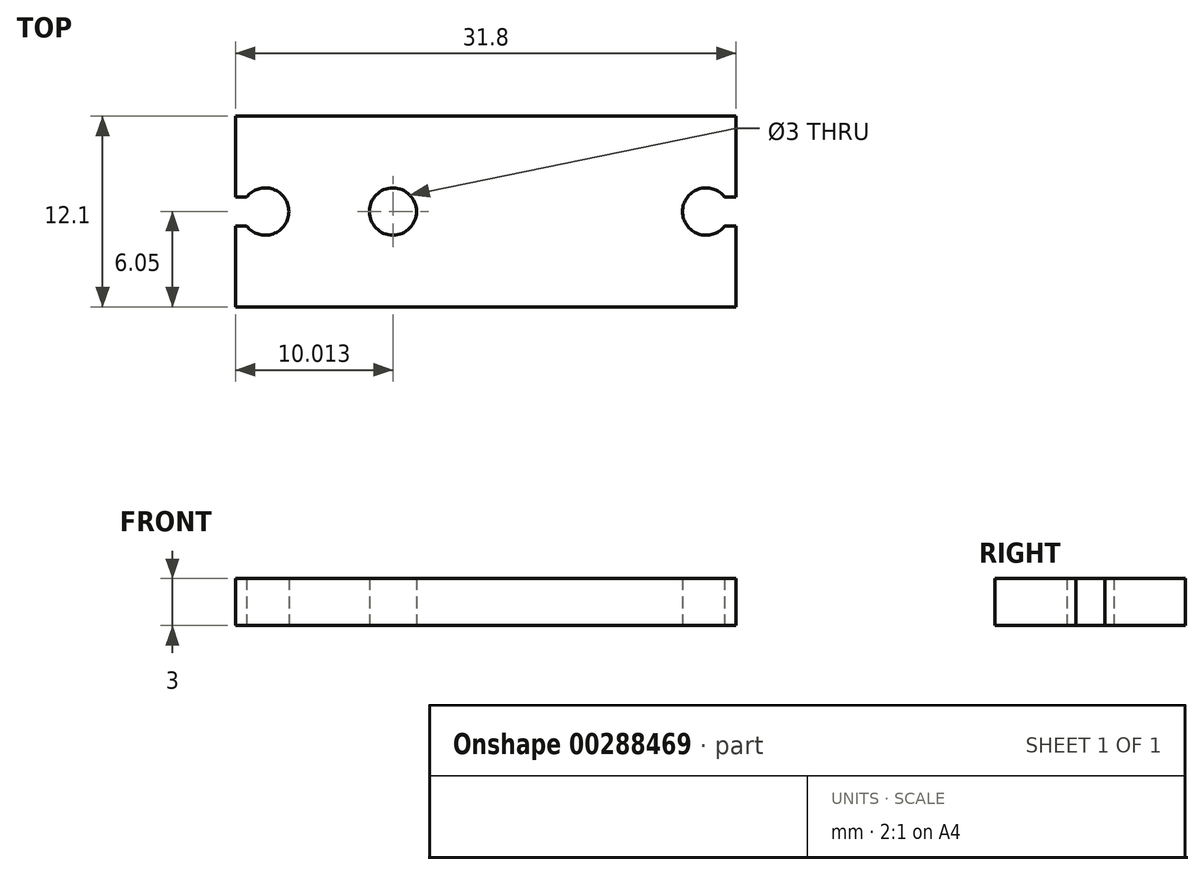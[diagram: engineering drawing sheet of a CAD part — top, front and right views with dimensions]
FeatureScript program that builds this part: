
annotation { "Feature Type Name" : "Feature", "Feature Type Description" : "" }
export const myFeature = defineFeature(function(context is Context, id is Id, definition is map)
    precondition{}
    {
        {
            var Q0;
            Q0=qCreatedBy(makeId("Top.planeOp"),FACE);
            var sketch = newSketch(context, id + "F0", { "sketchPlane" : qUnion([Q0])});
            skLineSegment(sketch, "E0.bottom", {"start": v(-15.9, 6.05) * mm, "end": v(15.9, 6.05) * mm});
            skLineSegment(sketch, "E0.top", {"start": v(-15.9, -6.05) * mm, "end": v(15.9, -6.05) * mm});
            skLineSegment(sketch, "E0.left", {"start": v(-15.9, 6.05) * mm, "end": v(-15.9, 0.93) * mm});
            skLineSegment(sketch, "E0.right", {"start": v(15.9, 6.05) * mm, "end": v(15.9, 0.93) * mm});
            skPoint(sketch, "E1", {"position": v(14, 0) * mm});
            skArc(sketch, "E2", {"start": v(15.18, 0.93) * mm, "mid": v(12.5, 0) * mm, "end": v(15.18, -0.93) * mm});
            skArc(sketch, "E3.MirrorC", {"start": v(-15.18, 0.93) * mm, "mid": v(-12.5, 0) * mm, "end": v(-15.18, -0.93) * mm});
            skPoint(sketch, "E4", {"position": v(-5.89, 0) * mm});
            skCircle(sketch, "E5", {"center": v(-5.89, 0) * mm, "radius": 1.5 * mm});
            skLineSegment(sketch, "E6", {"start": v(15.9, 0.93) * mm, "end": v(15.18, 0.93) * mm});
            skLineSegment(sketch, "E7.MirrorCS", {"start": v(15.9, -0.93) * mm, "end": v(15.18, -0.93) * mm});
            skPoint(sketch, "E8.orphan", {"position": v(14.9, 0.93) * mm});
            skPoint(sketch, "E9.orphan", {"position": v(14.9, -0.93) * mm});
            skLineSegment(sketch, "E10.MirrorCS", {"start": v(-15.9, -0.93) * mm, "end": v(-15.18, -0.93) * mm});
            skLineSegment(sketch, "E11.MirrorCS", {"start": v(-15.9, 0.93) * mm, "end": v(-15.18, 0.93) * mm});
            skLineSegment(sketch, "E12.trimOffspring", {"start": v(-15.9, -0.93) * mm, "end": v(-15.9, -6.05) * mm});
            skLineSegment(sketch, "E13.trimOffspring", {"start": v(15.9, -0.93) * mm, "end": v(15.9, -6.05) * mm});
            skSolve(sketch);
        }
        {
            var Q0;
            Q0=qSketchRegion(id+"F0",true);
            extrude(context, id + "F1", {"entities" : qUnion([Q0]), "depth" : 3 * mm});
        }
    });
